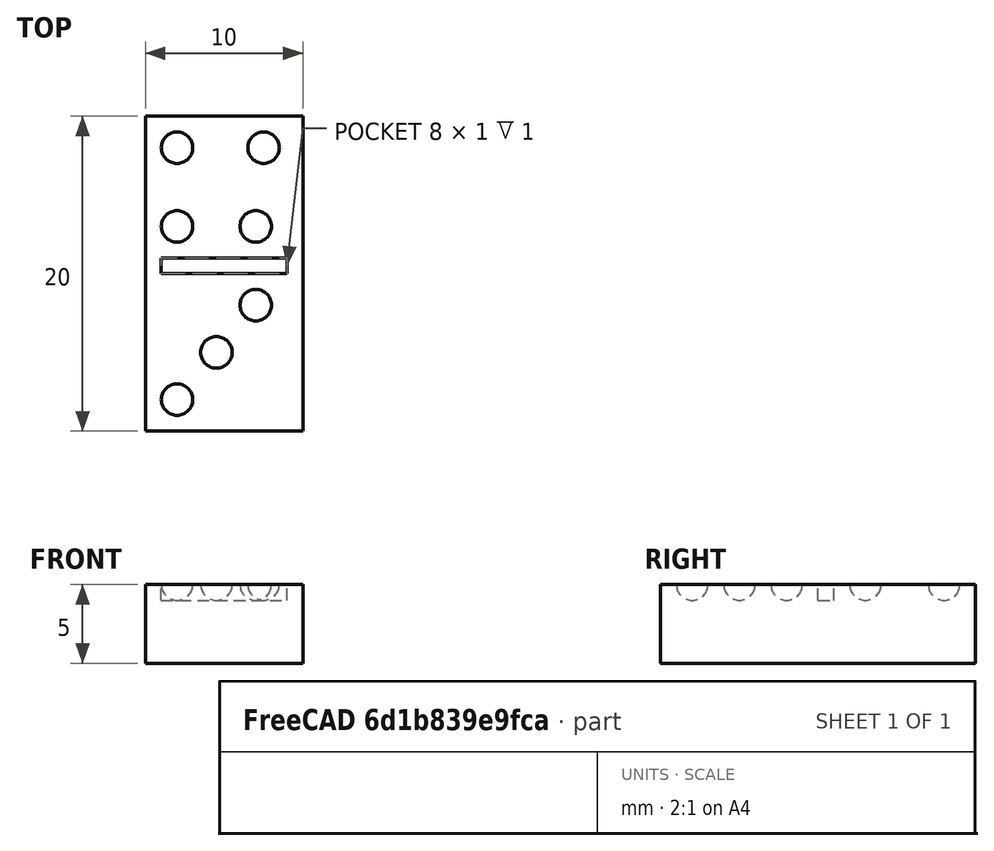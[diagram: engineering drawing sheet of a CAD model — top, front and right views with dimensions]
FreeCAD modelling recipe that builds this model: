
FCSTD DOCUMENT  (FreeCAD 0.20R29177 +426 (Git))
Label: Domino
License: All rights reserved
LicenseURL: http://en.wikipedia.org/wiki/All_rights_reserved
objects: Part::Sphere×8, Part::Box×2, Part::MultiFuse×1, Part::Cut×1
note: 12 computed .brp shape members not serialized (recipe doc carries the construction recipe); baked Part::Feature solids carry a one-line shape summary decoded from their .brp

FEATURE [Part::Box] Box  label="Cubo"
  AttacherType = Attacher::AttachEngine3D
  Height = 5
  Length = 10
  Width = 20
FEATURE [Part::Box] Box001  label="Cubo001"
  AttacherType = Attacher::AttachEngine3D
  Height = 1
  Length = 8
  Placement = pos=(1,10,4) rot=(0,0,1;0rad)
  Width = 1
FEATURE [Part::Sphere] Sphere  label="Esfera"
  Angle1 = -90
  Angle2 = 90
  Angle3 = 180
  AttacherType = Attacher::AttachEngine3D
  Placement = pos=(2,2,5) rot=(-1,0,0;1.5708rad)
  Radius = 1
FEATURE [Part::Sphere] Sphere001  label="Esfera001"
  Angle1 = -90
  Angle2 = 90
  Angle3 = 180
  AttacherType = Attacher::AttachEngine3D
  Placement = pos=(4.5,5,5) rot=(-1,0,0;1.5708rad)
  Radius = 1
FEATURE [Part::Sphere] Sphere002  label="Esfera002"
  Angle1 = -90
  Angle2 = 90
  Angle3 = 180
  AttacherType = Attacher::AttachEngine3D
  Placement = pos=(7,8,5) rot=(-1,0,0;1.5708rad)
  Radius = 1
FEATURE [Part::Sphere] Sphere003  label="Esfera003"
  Angle1 = -90
  Angle2 = 90
  Angle3 = 180
  AttacherType = Attacher::AttachEngine3D
  Placement = pos=(4.5,5,5) rot=(-1,0,0;1.5708rad)
  Radius = 1
FEATURE [Part::Sphere] Sphere004  label="Esfera004"
  Angle1 = -90
  Angle2 = 90
  Angle3 = 180
  AttacherType = Attacher::AttachEngine3D
  Placement = pos=(7.5,18,5) rot=(-1,0,0;1.5708rad)
  Radius = 1
FEATURE [Part::Sphere] Sphere005  label="Esfera005"
  Angle1 = -90
  Angle2 = 90
  Angle3 = 180
  AttacherType = Attacher::AttachEngine3D
  Placement = pos=(2,18,5) rot=(-1,0,0;1.5708rad)
  Radius = 1
FEATURE [Part::Sphere] Sphere006  label="Esfera006"
  Angle1 = -90
  Angle2 = 90
  Angle3 = 180
  AttacherType = Attacher::AttachEngine3D
  Placement = pos=(2,13,5) rot=(-1,0,0;1.5708rad)
  Radius = 1
FEATURE [Part::Sphere] Sphere007  label="Esfera007"
  Angle1 = -90
  Angle2 = 90
  Angle3 = 180
  AttacherType = Attacher::AttachEngine3D
  Placement = pos=(7,13,5) rot=(-1,0,0;1.5708rad)
  Radius = 1
FEATURE [Part::MultiFuse] Fusion
  Refine = true
  Shapes = -> [Box001,Sphere,Sphere002,Sphere001,Sphere003,Sphere004,Sphere005,Sphere006,Sphere007]
FEATURE [Part::Cut] Cut
  Base = -> Box
  Refine = true
  Tool = -> Fusion
